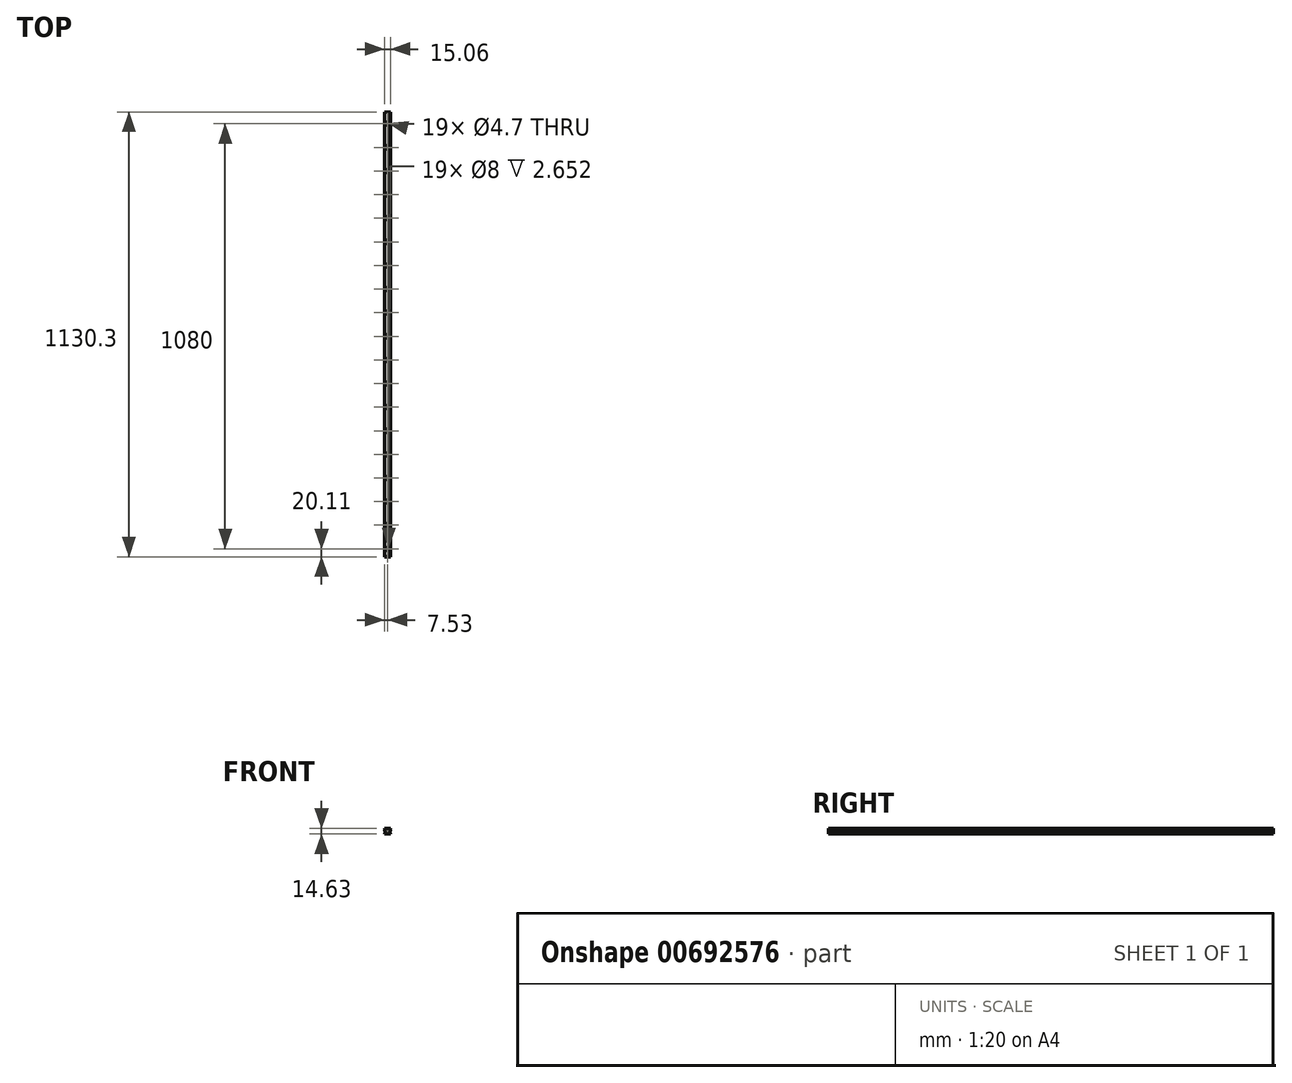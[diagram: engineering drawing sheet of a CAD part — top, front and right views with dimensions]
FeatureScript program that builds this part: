
annotation { "Feature Type Name" : "Feature", "Feature Type Description" : "" }
export const myFeature = defineFeature(function(context is Context, id is Id, definition is map)
    precondition{}
    {
        {
            var Q0;
            Q0=qCreatedBy(makeId("Front.planeOp"),FACE);
            var sketch = newSketch(context, id + "F0", { "sketchPlane" : qUnion([Q0])});
            skLineSegment(sketch, "E0.bottom", {"start": v(-7.53, -7.28) * mm, "end": v(7.53, -7.28) * mm});
            skLineSegment(sketch, "E0.top", {"start": v(-7.53, 7.35) * mm, "end": v(7.53, 7.35) * mm});
            skLineSegment(sketch, "E0.left", {"start": v(-7.53, -7.28) * mm, "end": v(-7.53, -5.04) * mm});
            skLineSegment(sketch, "E0.right", {"start": v(7.53, -7.28) * mm, "end": v(7.53, -5.04) * mm});
            skLineSegment(sketch, "E1.trimOffspring", {"start": v(-7.53, 5.64) * mm, "end": v(-7.53, 7.35) * mm});
            skLineSegment(sketch, "E2.trimOffspring", {"start": v(7.53, 5.64) * mm, "end": v(7.53, 7.35) * mm});
            skLineSegment(sketch, "E3", {"start": v(7.53, 0.5) * mm, "end": v(6.87, 0.5) * mm});
            skLineSegment(sketch, "E4", {"start": v(6.87, 0.5) * mm, "end": v(6.87, -5.04) * mm});
            skLineSegment(sketch, "E5", {"start": v(6.87, -5.04) * mm, "end": v(7.53, -5.04) * mm});
            skLineSegment(sketch, "E6", {"start": v(0, 7.35) * mm, "end": v(0, -7.28) * mm, "construction": true});
            skLineSegment(sketch, "E7.MirrorCS", {"start": v(-6.87, 0.5) * mm, "end": v(-6.87, -5.04) * mm});
            skLineSegment(sketch, "E8.MirrorCS", {"start": v(-7.53, 0.5) * mm, "end": v(-6.87, 0.5) * mm});
            skLineSegment(sketch, "E9.MirrorCS", {"start": v(-6.87, -5.04) * mm, "end": v(-7.53, -5.04) * mm});
            skLineSegment(sketch, "E10.trimOffspring", {"start": v(7.53, 0.5) * mm, "end": v(7.53, 3.36) * mm});
            skLineSegment(sketch, "E11.trimOffspring", {"start": v(-7.53, 0.5) * mm, "end": v(-7.53, 3.36) * mm});
            skLineSegment(sketch, "E12.bottom", {"start": v(-5.99, 5.03) * mm, "end": v(-6.92, 5.03) * mm});
            skLineSegment(sketch, "E12.top", {"start": v(-5.99, 3.97) * mm, "end": v(-6.92, 3.97) * mm});
            skLineSegment(sketch, "E12.left", {"start": v(-5.99, 5.03) * mm, "end": v(-5.99, 3.97) * mm});
            skLineSegment(sketch, "E13", {"start": v(-7.53, 5.64) * mm, "end": v(-6.92, 5.03) * mm});
            skLineSegment(sketch, "E14", {"start": v(-7.53, 3.36) * mm, "end": v(-6.92, 3.97) * mm});
            skLineSegment(sketch, "E15.MirrorCS", {"start": v(5.99, 5.03) * mm, "end": v(6.92, 5.03) * mm});
            skLineSegment(sketch, "E16.MirrorCS", {"start": v(7.53, 3.36) * mm, "end": v(6.92, 3.97) * mm});
            skLineSegment(sketch, "E17.MirrorCS", {"start": v(5.99, 3.97) * mm, "end": v(6.92, 3.97) * mm});
            skLineSegment(sketch, "E18.MirrorCS", {"start": v(5.99, 5.03) * mm, "end": v(5.99, 3.97) * mm});
            skLineSegment(sketch, "E19.MirrorCS", {"start": v(7.53, 5.64) * mm, "end": v(6.92, 5.03) * mm});
            skSolve(sketch);
        }
        {
            var Q0;
            Q0=makeQuery(id+"F0.imprint","IMPRINT",FACE,{"disambiguationData":[TD([[makeQuery(id+"F0.imprint","IMPRINT",EDGE,{"derivedFrom":sQuery(id+"F0.wireOp",EDGE,"E0.bottom")}),1.0]])]});
            extrude(context, id + "F1", {"entities" : qUnion([Q0]), "depth" : 1130.3 * mm, "offsetDistance" : 25.4 * mm});
        }
        {
            var Q0;
            Q0=makeQuery(id+"F1.opExtrude","SWEPT_FACE",FACE,{"disambiguationData":[OSD([sQuery(id+"F0.wireOp",EDGE,"E0.top")])]});
            var sketch = newSketch(context, id + "F2", { "sketchPlane" : qUnion([Q0])});
            skCircle(sketch, "E20", {"center": v(0, -1110.19) * mm, "radius": 2.35 * mm});
            skPoint(sketch, "E20.centerSnap0", {"position": v(0, -1130.3) * mm});
            skCircle(sketch, "E21", {"center": v(0, -1110.19) * mm, "radius": 4 * mm});
            skCircle(sketch, "E22.0.1.0", {"center": v(0, -1050.19) * mm, "radius": 2.35 * mm});
            skCircle(sketch, "E22.0.1.1", {"center": v(0, -1050.19) * mm, "radius": 4 * mm});
            skCircle(sketch, "E22.0.2.0", {"center": v(0, -990.19) * mm, "radius": 2.35 * mm});
            skCircle(sketch, "E22.0.2.1", {"center": v(0, -990.19) * mm, "radius": 4 * mm});
            skCircle(sketch, "E22.0.3.0", {"center": v(0, -930.19) * mm, "radius": 2.35 * mm});
            skCircle(sketch, "E22.0.3.1", {"center": v(0, -930.19) * mm, "radius": 4 * mm});
            skCircle(sketch, "E22.0.4.0", {"center": v(0, -870.19) * mm, "radius": 2.35 * mm});
            skCircle(sketch, "E22.0.4.1", {"center": v(0, -870.19) * mm, "radius": 4 * mm});
            skCircle(sketch, "E22.0.5.0", {"center": v(0, -810.19) * mm, "radius": 2.35 * mm});
            skCircle(sketch, "E22.0.5.1", {"center": v(0, -810.19) * mm, "radius": 4 * mm});
            skCircle(sketch, "E22.0.6.0", {"center": v(0, -750.19) * mm, "radius": 2.35 * mm});
            skCircle(sketch, "E22.0.6.1", {"center": v(0, -750.19) * mm, "radius": 4 * mm});
            skCircle(sketch, "E22.0.7.0", {"center": v(0, -690.19) * mm, "radius": 2.35 * mm});
            skCircle(sketch, "E22.0.7.1", {"center": v(0, -690.19) * mm, "radius": 4 * mm});
            skCircle(sketch, "E22.0.8.0", {"center": v(0, -630.19) * mm, "radius": 2.35 * mm});
            skCircle(sketch, "E22.0.8.1", {"center": v(0, -630.19) * mm, "radius": 4 * mm});
            skCircle(sketch, "E22.0.9.0", {"center": v(0, -570.19) * mm, "radius": 2.35 * mm});
            skCircle(sketch, "E22.0.9.1", {"center": v(0, -570.19) * mm, "radius": 4 * mm});
            skCircle(sketch, "E22.0.10.0", {"center": v(0, -510.19) * mm, "radius": 2.35 * mm});
            skCircle(sketch, "E22.0.10.1", {"center": v(0, -510.19) * mm, "radius": 4 * mm});
            skCircle(sketch, "E22.0.11.0", {"center": v(0, -450.19) * mm, "radius": 2.35 * mm});
            skCircle(sketch, "E22.0.11.1", {"center": v(0, -450.19) * mm, "radius": 4 * mm});
            skCircle(sketch, "E22.0.12.0", {"center": v(0, -390.19) * mm, "radius": 2.35 * mm});
            skCircle(sketch, "E22.0.12.1", {"center": v(0, -390.19) * mm, "radius": 4 * mm});
            skCircle(sketch, "E22.0.13.0", {"center": v(0, -330.19) * mm, "radius": 2.35 * mm});
            skCircle(sketch, "E22.0.13.1", {"center": v(0, -330.19) * mm, "radius": 4 * mm});
            skCircle(sketch, "E22.0.14.0", {"center": v(0, -270.19) * mm, "radius": 2.35 * mm});
            skCircle(sketch, "E22.0.14.1", {"center": v(0, -270.19) * mm, "radius": 4 * mm});
            skCircle(sketch, "E22.0.15.0", {"center": v(0, -210.19) * mm, "radius": 2.35 * mm});
            skCircle(sketch, "E22.0.15.1", {"center": v(0, -210.19) * mm, "radius": 4 * mm});
            skCircle(sketch, "E22.0.16.0", {"center": v(0, -150.19) * mm, "radius": 2.35 * mm});
            skCircle(sketch, "E22.0.16.1", {"center": v(0, -150.19) * mm, "radius": 4 * mm});
            skCircle(sketch, "E22.0.17.0", {"center": v(0, -90.19) * mm, "radius": 2.35 * mm});
            skCircle(sketch, "E22.0.17.1", {"center": v(0, -90.19) * mm, "radius": 4 * mm});
            skCircle(sketch, "E22.0.18.0", {"center": v(0, -30.19) * mm, "radius": 2.35 * mm});
            skCircle(sketch, "E22.0.18.1", {"center": v(0, -30.19) * mm, "radius": 4 * mm});
            skLineSegment(sketch, "E22.direction1", {"start": v(0, -1110.19) * mm, "end": v(25.4, -1110.19) * mm, "construction": true});
            skLineSegment(sketch, "E22.direction2", {"start": v(0, -1110.19) * mm, "end": v(0, -1050.19) * mm, "construction": true});
            skSolve(sketch);
        }
        {
            var Q0;
            Q0=makeQuery(id+"F2.imprint","IMPRINT",FACE,{"disambiguationData":[TD([[makeQuery(id+"F2.imprint","IMPRINT",EDGE,{"derivedFrom":sQuery(id+"F2.wireOp",EDGE,"E22.0.18.0")}),1.0]])]});
            var Q1;
            Q1=makeQuery(id+"F2.imprint","IMPRINT",FACE,{"disambiguationData":[TD([[makeQuery(id+"F2.imprint","IMPRINT",EDGE,{"derivedFrom":sQuery(id+"F2.wireOp",EDGE,"E22.0.17.0")}),1.0]])]});
            var Q2;
            Q2=makeQuery(id+"F2.imprint","IMPRINT",FACE,{"disambiguationData":[TD([[makeQuery(id+"F2.imprint","IMPRINT",EDGE,{"derivedFrom":sQuery(id+"F2.wireOp",EDGE,"E22.0.16.0")}),1.0]])]});
            var Q3;
            Q3=makeQuery(id+"F2.imprint","IMPRINT",FACE,{"disambiguationData":[TD([[makeQuery(id+"F2.imprint","IMPRINT",EDGE,{"derivedFrom":sQuery(id+"F2.wireOp",EDGE,"E22.0.15.0")}),1.0]])]});
            var Q4;
            Q4=makeQuery(id+"F2.imprint","IMPRINT",FACE,{"disambiguationData":[TD([[makeQuery(id+"F2.imprint","IMPRINT",EDGE,{"derivedFrom":sQuery(id+"F2.wireOp",EDGE,"E22.0.14.0")}),1.0]])]});
            var Q5;
            Q5=makeQuery(id+"F2.imprint","IMPRINT",FACE,{"disambiguationData":[TD([[makeQuery(id+"F2.imprint","IMPRINT",EDGE,{"derivedFrom":sQuery(id+"F2.wireOp",EDGE,"E22.0.13.0")}),1.0]])]});
            var Q6;
            Q6=makeQuery(id+"F2.imprint","IMPRINT",FACE,{"disambiguationData":[TD([[makeQuery(id+"F2.imprint","IMPRINT",EDGE,{"derivedFrom":sQuery(id+"F2.wireOp",EDGE,"E22.0.12.0")}),1.0]])]});
            var Q7;
            Q7=makeQuery(id+"F2.imprint","IMPRINT",FACE,{"disambiguationData":[TD([[makeQuery(id+"F2.imprint","IMPRINT",EDGE,{"derivedFrom":sQuery(id+"F2.wireOp",EDGE,"E22.0.11.0")}),1.0]])]});
            var Q8;
            Q8=makeQuery(id+"F2.imprint","IMPRINT",FACE,{"disambiguationData":[TD([[makeQuery(id+"F2.imprint","IMPRINT",EDGE,{"derivedFrom":sQuery(id+"F2.wireOp",EDGE,"E22.0.10.0")}),1.0]])]});
            var Q9;
            Q9=makeQuery(id+"F2.imprint","IMPRINT",FACE,{"disambiguationData":[TD([[makeQuery(id+"F2.imprint","IMPRINT",EDGE,{"derivedFrom":sQuery(id+"F2.wireOp",EDGE,"E22.0.9.0")}),1.0]])]});
            var Q10;
            Q10=makeQuery(id+"F2.imprint","IMPRINT",FACE,{"disambiguationData":[TD([[makeQuery(id+"F2.imprint","IMPRINT",EDGE,{"derivedFrom":sQuery(id+"F2.wireOp",EDGE,"E22.0.8.0")}),1.0]])]});
            var Q11;
            Q11=makeQuery(id+"F2.imprint","IMPRINT",FACE,{"disambiguationData":[TD([[makeQuery(id+"F2.imprint","IMPRINT",EDGE,{"derivedFrom":sQuery(id+"F2.wireOp",EDGE,"E22.0.7.0")}),1.0]])]});
            var Q12;
            Q12=makeQuery(id+"F2.imprint","IMPRINT",FACE,{"disambiguationData":[TD([[makeQuery(id+"F2.imprint","IMPRINT",EDGE,{"derivedFrom":sQuery(id+"F2.wireOp",EDGE,"E22.0.6.0")}),1.0]])]});
            var Q13;
            Q13=makeQuery(id+"F2.imprint","IMPRINT",FACE,{"disambiguationData":[TD([[makeQuery(id+"F2.imprint","IMPRINT",EDGE,{"derivedFrom":sQuery(id+"F2.wireOp",EDGE,"E22.0.5.0")}),1.0]])]});
            var Q14;
            Q14=makeQuery(id+"F2.imprint","IMPRINT",FACE,{"disambiguationData":[TD([[makeQuery(id+"F2.imprint","IMPRINT",EDGE,{"derivedFrom":sQuery(id+"F2.wireOp",EDGE,"E22.0.4.0")}),1.0]])]});
            var Q15;
            Q15=makeQuery(id+"F2.imprint","IMPRINT",FACE,{"disambiguationData":[TD([[makeQuery(id+"F2.imprint","IMPRINT",EDGE,{"derivedFrom":sQuery(id+"F2.wireOp",EDGE,"E22.0.3.0")}),1.0]])]});
            var Q16;
            Q16=makeQuery(id+"F2.imprint","IMPRINT",FACE,{"disambiguationData":[TD([[makeQuery(id+"F2.imprint","IMPRINT",EDGE,{"derivedFrom":sQuery(id+"F2.wireOp",EDGE,"E22.0.2.0")}),1.0]])]});
            var Q17;
            Q17=makeQuery(id+"F2.imprint","IMPRINT",FACE,{"disambiguationData":[TD([[makeQuery(id+"F2.imprint","IMPRINT",EDGE,{"derivedFrom":sQuery(id+"F2.wireOp",EDGE,"E22.0.1.0")}),1.0]])]});
            var Q18;
            Q18=makeQuery(id+"F2.imprint","IMPRINT",FACE,{"disambiguationData":[TD([[makeQuery(id+"F2.imprint","IMPRINT",EDGE,{"derivedFrom":sQuery(id+"F2.wireOp",EDGE,"E20")}),1.0]])]});
            extrude(context, id + "F3", {"entities" : qUnion([Q0, Q1, Q2, Q3, Q4, Q5, Q6, Q7, Q8, Q9, Q10, Q11, Q12, Q13, Q14, Q15, Q16, Q17, Q18]), "operationType" : NewBodyOperationType.REMOVE, "oppositeDirection" : true, "depth" : 25.4 * mm, "offsetDistance" : 25.4 * mm});
        }
        {
            var Q0;
            Q0=makeQuery(id+"F2.imprint","IMPRINT",FACE,{"disambiguationData":[TD([[makeQuery(id+"F2.imprint","IMPRINT",EDGE,{"derivedFrom":sQuery(id+"F2.wireOp",EDGE,"E20")}),-1.0]])]});
            var Q1;
            Q1=makeQuery(id+"F2.imprint","IMPRINT",FACE,{"disambiguationData":[TD([[makeQuery(id+"F2.imprint","IMPRINT",EDGE,{"derivedFrom":sQuery(id+"F2.wireOp",EDGE,"E22.0.1.0")}),-1.0]])]});
            var Q2;
            Q2=makeQuery(id+"F2.imprint","IMPRINT",FACE,{"disambiguationData":[TD([[makeQuery(id+"F2.imprint","IMPRINT",EDGE,{"derivedFrom":sQuery(id+"F2.wireOp",EDGE,"E22.0.2.0")}),-1.0]])]});
            var Q3;
            Q3=makeQuery(id+"F2.imprint","IMPRINT",FACE,{"disambiguationData":[TD([[makeQuery(id+"F2.imprint","IMPRINT",EDGE,{"derivedFrom":sQuery(id+"F2.wireOp",EDGE,"E22.0.3.0")}),-1.0]])]});
            var Q4;
            Q4=makeQuery(id+"F2.imprint","IMPRINT",FACE,{"disambiguationData":[TD([[makeQuery(id+"F2.imprint","IMPRINT",EDGE,{"derivedFrom":sQuery(id+"F2.wireOp",EDGE,"E22.0.4.0")}),-1.0]])]});
            var Q5;
            Q5=makeQuery(id+"F2.imprint","IMPRINT",FACE,{"disambiguationData":[TD([[makeQuery(id+"F2.imprint","IMPRINT",EDGE,{"derivedFrom":sQuery(id+"F2.wireOp",EDGE,"E22.0.5.0")}),-1.0]])]});
            var Q6;
            Q6=makeQuery(id+"F2.imprint","IMPRINT",FACE,{"disambiguationData":[TD([[makeQuery(id+"F2.imprint","IMPRINT",EDGE,{"derivedFrom":sQuery(id+"F2.wireOp",EDGE,"E22.0.6.0")}),-1.0]])]});
            var Q7;
            Q7=makeQuery(id+"F2.imprint","IMPRINT",FACE,{"disambiguationData":[TD([[makeQuery(id+"F2.imprint","IMPRINT",EDGE,{"derivedFrom":sQuery(id+"F2.wireOp",EDGE,"E22.0.7.0")}),-1.0]])]});
            var Q8;
            Q8=makeQuery(id+"F2.imprint","IMPRINT",FACE,{"disambiguationData":[TD([[makeQuery(id+"F2.imprint","IMPRINT",EDGE,{"derivedFrom":sQuery(id+"F2.wireOp",EDGE,"E22.0.8.0")}),-1.0]])]});
            var Q9;
            Q9=makeQuery(id+"F2.imprint","IMPRINT",FACE,{"disambiguationData":[TD([[makeQuery(id+"F2.imprint","IMPRINT",EDGE,{"derivedFrom":sQuery(id+"F2.wireOp",EDGE,"E22.0.9.0")}),-1.0]])]});
            var Q10;
            Q10=makeQuery(id+"F2.imprint","IMPRINT",FACE,{"disambiguationData":[TD([[makeQuery(id+"F2.imprint","IMPRINT",EDGE,{"derivedFrom":sQuery(id+"F2.wireOp",EDGE,"E22.0.10.0")}),-1.0]])]});
            var Q11;
            Q11=makeQuery(id+"F2.imprint","IMPRINT",FACE,{"disambiguationData":[TD([[makeQuery(id+"F2.imprint","IMPRINT",EDGE,{"derivedFrom":sQuery(id+"F2.wireOp",EDGE,"E22.0.11.0")}),-1.0]])]});
            var Q12;
            Q12=makeQuery(id+"F2.imprint","IMPRINT",FACE,{"disambiguationData":[TD([[makeQuery(id+"F2.imprint","IMPRINT",EDGE,{"derivedFrom":sQuery(id+"F2.wireOp",EDGE,"E22.0.12.0")}),-1.0]])]});
            var Q13;
            Q13=makeQuery(id+"F2.imprint","IMPRINT",FACE,{"disambiguationData":[TD([[makeQuery(id+"F2.imprint","IMPRINT",EDGE,{"derivedFrom":sQuery(id+"F2.wireOp",EDGE,"E22.0.13.0")}),-1.0]])]});
            var Q14;
            Q14=makeQuery(id+"F2.imprint","IMPRINT",FACE,{"disambiguationData":[TD([[makeQuery(id+"F2.imprint","IMPRINT",EDGE,{"derivedFrom":sQuery(id+"F2.wireOp",EDGE,"E22.0.14.0")}),-1.0]])]});
            var Q15;
            Q15=makeQuery(id+"F2.imprint","IMPRINT",FACE,{"disambiguationData":[TD([[makeQuery(id+"F2.imprint","IMPRINT",EDGE,{"derivedFrom":sQuery(id+"F2.wireOp",EDGE,"E22.0.15.0")}),-1.0]])]});
            var Q16;
            Q16=makeQuery(id+"F2.imprint","IMPRINT",FACE,{"disambiguationData":[TD([[makeQuery(id+"F2.imprint","IMPRINT",EDGE,{"derivedFrom":sQuery(id+"F2.wireOp",EDGE,"E22.0.16.0")}),-1.0]])]});
            var Q17;
            Q17=makeQuery(id+"F2.imprint","IMPRINT",FACE,{"disambiguationData":[TD([[makeQuery(id+"F2.imprint","IMPRINT",EDGE,{"derivedFrom":sQuery(id+"F2.wireOp",EDGE,"E22.0.17.0")}),-1.0]])]});
            var Q18;
            Q18=makeQuery(id+"F2.imprint","IMPRINT",FACE,{"disambiguationData":[TD([[makeQuery(id+"F2.imprint","IMPRINT",EDGE,{"derivedFrom":sQuery(id+"F2.wireOp",EDGE,"E22.0.18.0")}),-1.0]])]});
            extrude(context, id + "F4", {"entities" : qUnion([Q0, Q1, Q2, Q3, Q4, Q5, Q6, Q7, Q8, Q9, Q10, Q11, Q12, Q13, Q14, Q15, Q16, Q17, Q18]), "operationType" : NewBodyOperationType.REMOVE, "oppositeDirection" : true, "depth" : 3.16 * mm, "offsetDistance" : 25.4 * mm});
        }
        {
            var Q0;
            Q0=makeQuery(id+"F1.opExtrude","SWEPT_FACE",FACE,{"disambiguationData":[OSD([sQuery(id+"F0.wireOp",EDGE,"E0.top")])]});
            var Q1;
            Q1=makeQuery(id+"F1.opExtrude","SWEPT_FACE",FACE,{"disambiguationData":[OSD([sQuery(id+"F0.wireOp",EDGE,"E0.bottom")])]});
            chamfer(context, id + "F5", {"entities" : qUnion([Q0, Q1]), "width" : 0.5 * mm, "tangentPropagation" : true});
        }
    });
